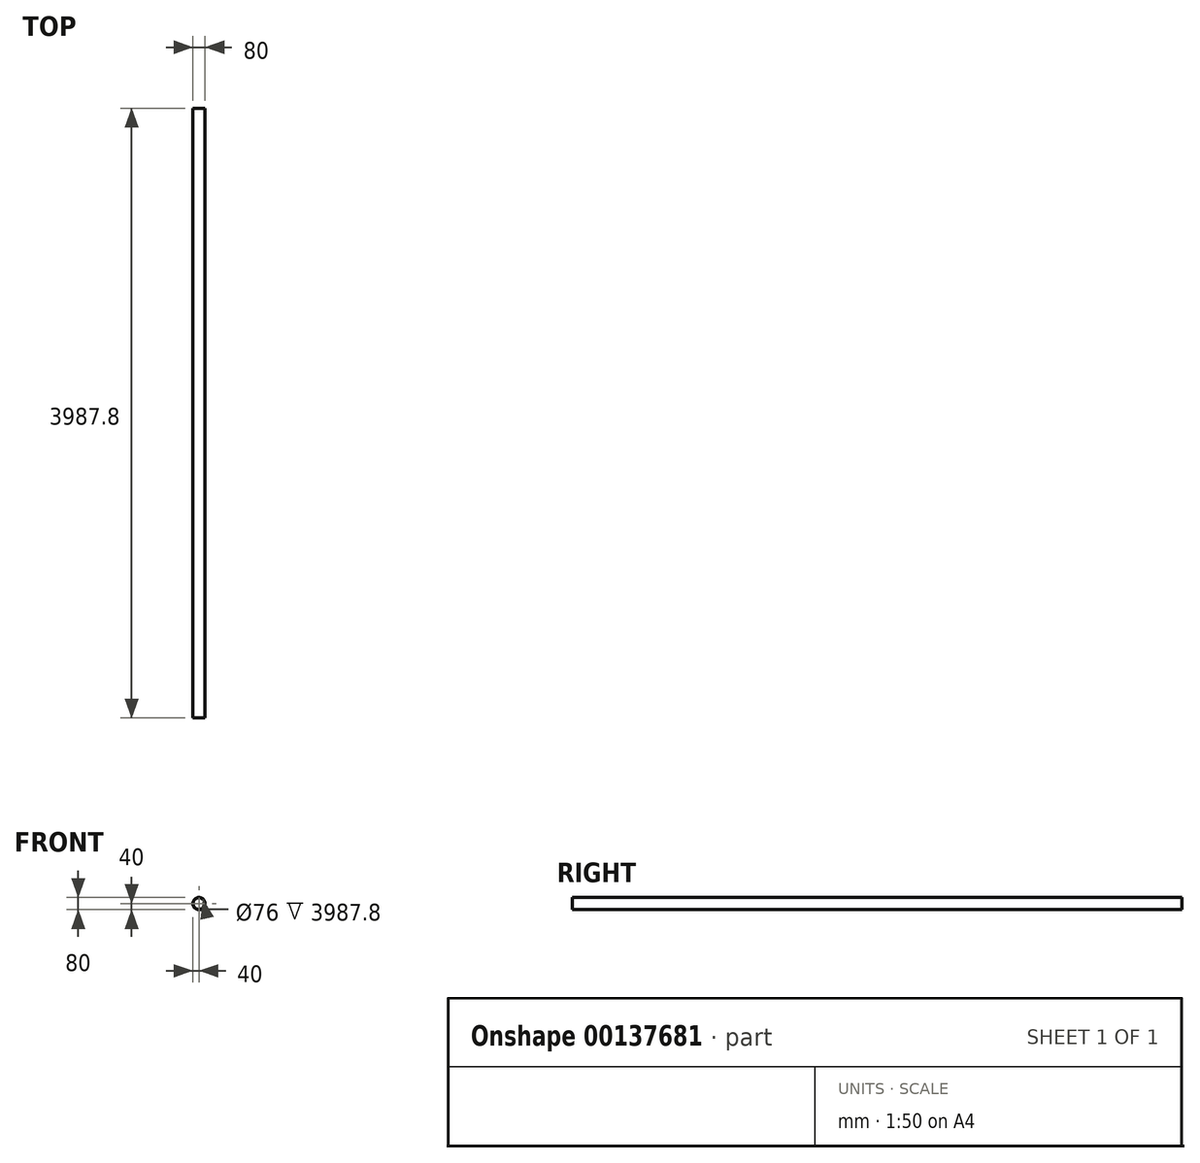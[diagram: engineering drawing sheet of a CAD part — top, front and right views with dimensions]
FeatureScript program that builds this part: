
annotation { "Feature Type Name" : "Feature", "Feature Type Description" : "" }
export const myFeature = defineFeature(function(context is Context, id is Id, definition is map)
    precondition{}
    {
        {
            var Q0;
            Q0=qCreatedBy(makeId("Front.planeOp"),FACE);
            var sketch = newSketch(context, id + "F0", { "sketchPlane" : qUnion([Q0])});
            skCircle(sketch, "E0", {"center": v(0, 0) * mm, "radius": 40 * mm});
            skCircle(sketch, "E1", {"center": v(0, 0) * mm, "radius": 38 * mm});
            skSolve(sketch);
        }
        {
            var Q0;
            Q0=makeQuery(id+"F0.imprint","IMPRINT",FACE,{"disambiguationData":[TD([[makeQuery(id+"F0.imprint","IMPRINT",EDGE,{"derivedFrom":sQuery(id+"F0.wireOp",EDGE,"E0")}),1.0]])]});
            var Q1;
            Q1=sQuery(id+"F0.wireOp",EDGE,"E1");
            var Q2;
            Q2=sQuery(id+"F0.wireOp",EDGE,"E0");
            extrude(context, id + "F1", {"entities" : qUnion([Q0]), "surfaceEntities" : qUnion([Q1, Q2]), "depth" : 3987.8 * mm, "offsetDistance" : 25 * mm});
        }
    });
